# Revit family: Sarlam_Lighting_Bollard_light_Chartres_Infini_T2_Vandal_resistant_Diam_435mm_3000Lm
name_source: partatom
category: Luminaires
units: mm (PartAtom-declared; Revit-internal decimal feet)

## family parameters
Basée sur le plan de construction = Non
Cote de connecteur circulaire = Utiliser le diamètre
Couper avec des vides une fois chargée = Non
Partagée = Non
Point de calcul de pièce = Non
Source d'éclairage = Non
Toujours verticalement = Oui
Type d'élément = Normal

## types (16) — shared parameters
Colour rendering index CRI = 80-89
Colour temperature K MAX = 4000
Colour temperature K MIN = 4000
Effective luminous flux lm = 3000
Fabricant = LEGRAND
General Conditions of Use = https://export.legrand.com
Height/depth = 90 mm  [stored 0.295276 ft]
Lamp holder = None
Lamp power at multiwatt = 21/39W
Lamp type = LED not exchangeable
Length = 435 mm  [stored 1.42717 ft]
Light sharing = Symmetric
Material housing = Plastique
Nominal voltage (Un) V MAX = 253
Nominal voltage (Un) V MIN = 207
Outer diameter = 435 mm  [stored 1.42717 ft]
Protection Class = II
Radiation angle = Open beam
Type of control gear = LED operating device current-controlled
URL = http://www.legrandoc.com
URL Bulkhead = http://www.legrandoc.com
Voltage type = AC
Width = 435 mm  [stored 1.42717 ft]
zero-valued in all types: Elévation par défaut, Nominal current mA MAX, Nominal current mA MIN, System power W

## per-type parameters (varying)
| type | Bollard light Height | Bulkhead | Colour housing | Degree of protection (IP) | Description | Impact strength (IK) | Modèle | Type of dimming | With light sensor | With movement sensor | leg Height |
| Bollard light 600 + ON/OFF WHITE | 600 mm | Legrand-Lighting-Bulkhead-Chartres Infini-T2 Vandal resistant-Diam 435mm-3000Lm : ON/OFF WHITE | LEGRAND - White | IP55 | BOLLARD LIGHT CHARTRES INFINI HEIGHT 600 + CHARTRES INFINI 3000LM 4000K AV ON/OFF WHITE | IK10 | SL-532030 + SL-532015 | Not dimmable | Non | Non | 524 mm |
| Bollard light 1200 + ON/OFF WHITE | 1200 mm | Legrand-Lighting-Bulkhead-Chartres Infini-T2 Vandal resistant-Diam 435mm-3000Lm : ON/OFF WHITE | LEGRAND - White | IP55 | BOLLARD LIGHT CHARTRES INFINI HEIGHT 1200 + CHARTRES INFINI 3000LM 4000K AV ON/OFF WHITE | IK10 | SL-532033 + SL-532015 | Not dimmable | Non | Non | 1124 mm  [stored 3.68766 ft] |
| Bollard light 600 + ON/OFF ANTHRACITE | 600 mm | Legrand-Lighting-Bulkhead-Chartres Infini-T2 Vandal resistant-Diam 435mm-3000Lm : ON/OFF ANTHRACITE | LEGRAND - Anthracite | IP55 | BOLLARD LIGHT CHARTRES INFINI HEIGHT 600 + CHARTRES INFINI 3000LM 4000K AV ON/OFF BLACK | IK10 | SL-532031 + SL-532016 | Not dimmable | Non | Non | 524 mm |
| Bollard light 1200 + ON/OFF ANTHRACITE | 1200 mm | Legrand-Lighting-Bulkhead-Chartres Infini-T2 Vandal resistant-Diam 435mm-3000Lm : ON/OFF ANTHRACITE | LEGRAND - Anthracite | IP55 | BOLLARD LIGHT CHARTRES INFINI HEIGHT 1200 + CHARTRES INFINI 3000LM 4000K AV ON/OFF BLACK | IK10 | SL-532034 + SL-532016 | Not dimmable | Non | Non | 1124 mm  [stored 3.68766 ft] |
| Bollard light 600 + ON/OFF GREY METAL | 600 mm | Legrand-Lighting-Bulkhead-Chartres Infini-T2 Vandal resistant-Diam 435mm-3000Lm : ON/OFF GREY METAL | LEGRAND - Grey | IP55 | BOLLARD LIGHT CHARTRES INFINI HEIGHT 600 + CHARTRES INFINI 3000LM 4000K AV ON/OFF SILVER | IK10 | SL-532032 + SL-532017 | Not dimmable | Non | Non | 524 mm |
| Bollard light 1200 + ON/OFF GREY METAL | 1200 mm | Legrand-Lighting-Bulkhead-Chartres Infini-T2 Vandal resistant-Diam 435mm-3000Lm : ON/OFF GREY METAL | LEGRAND - Grey | IP55 | BOLLARD LIGHT CHARTRES INFINI HEIGHT 1200 + CHARTRES INFINI 3000LM 4000K AV ON/OFF SILVER | IK10 | SL-532035 + SL-532017 | Not dimmable | Non | Non | 1124 mm  [stored 3.68766 ft] |
| Bollard light 600 + With microwave sensor WHITE | 600 mm | Legrand-Lighting-Bulkhead-Chartres Infini-T2 Vandal resistant-Diam 435mm-3000Lm : With microwave sensor WHITE | LEGRAND - White | IP55 | BOLLARD LIGHT CHARTRES INFINI HEIGHT 600 + CHARTRES INFINI 3000LM 4000K AV HF DETECTION WHITE | IK10 | SL-532030 + SL-532055 | Other | Oui | Oui | 524 mm |
| Bollard light 1200 + With microwave sensor WHITE | 1200 mm | Legrand-Lighting-Bulkhead-Chartres Infini-T2 Vandal resistant-Diam 435mm-3000Lm : With microwave sensor WHITE | LEGRAND - White | IP55 | BOLLARD LIGHT CHARTRES INFINI HEIGHT 1200 + CHARTRES INFINI 3000LM 4000K AV HF DETECTION WHITE | IK10 | SL-532033 + SL-532055 | Other | Oui | Oui | 1124 mm  [stored 3.68766 ft] |
| Bollard light 600 + With microwave sensor ANTHRACITE | 600 mm | Legrand-Lighting-Bulkhead-Chartres Infini-T2 Vandal resistant-Diam 435mm-3000Lm : With microwave sensor ANTHRACITE | LEGRAND - Anthracite | IP55 | BOLLARD LIGHT CHARTRES INFINI HEIGHT 600 + CHARTRES INFINI 3000LM 4000K AV HF DETECTION BLACK | IK10 | SL-532031 + SL-532056 | Other | Oui | Oui | 524 mm |
| Bollard light 1200 + With microwave sensor ANTHRACITE | 1200 mm | Legrand-Lighting-Bulkhead-Chartres Infini-T2 Vandal resistant-Diam 435mm-3000Lm : With microwave sensor ANTHRACITE | LEGRAND - Anthracite | IP55 | BOLLARD LIGHT CHARTRES INFINI HEIGHT 1200 + CHARTRES INFINI 3000LM 4000K AV HF DETECTION BLACK | IK10 | SL-532034 + SL-532056 | Other | Oui | Oui | 1124 mm  [stored 3.68766 ft] |
| Bollard light 600 + With microwave sensor GREY METAL | 600 mm | Legrand-Lighting-Bulkhead-Chartres Infini-T2 Vandal resistant-Diam 435mm-3000Lm : With microwave sensor GREY METAL | LEGRAND - Grey | IP55 | BOLLARD LIGHT CHARTRES INFINI HEIGHT 600 + CHARTRES INFINI 3000LM 4000K AV HF DETECTION SILVER | IK10 | SL-532032 + SL-532057 | Other | Oui | Oui | 524 mm |
| Bollard light 1200 + With microwave sensor GREY METAL | 1200 mm | Legrand-Lighting-Bulkhead-Chartres Infini-T2 Vandal resistant-Diam 435mm-3000Lm : With microwave sensor GREY METAL | LEGRAND - Grey | IP55 | BOLLARD LIGHT CHARTRES INFINI HEIGHT 1200 + CHARTRES INFINI 3000LM 4000K AV HF DETECTION SILVER | IK10 | SL-532035 + SL-532057 | Other | Oui | Oui | 1124 mm  [stored 3.68766 ft] |
| Bollard light 1200 + vandal resistant - With microwave sensor | 1200 mm | Legrand-Lighting-Bulkhead-Chartres Infini-T2 Vandal resistant-Diam 435mm-3000Lm : Vandal resistant - With microwave sensor | LEGRAND - White | IP66 | BOLLARD LIGHT CHARTRES INFINI HEIGHT 1200 + CHARTRES INFINI 3000LM 4000K SOLIROC HF DETECTION WHITE | >IK10 | SL-532033 + SL-532099 | Other | Oui | Oui | 1124 mm  [stored 3.68766 ft] |
| Bollard light 600 + vandal resistant - With microwave sensor | 600 mm | Legrand-Lighting-Bulkhead-Chartres Infini-T2 Vandal resistant-Diam 435mm-3000Lm : Vandal resistant - With microwave sensor | LEGRAND - White | IP66 | BOLLARD LIGHT CHARTRES INFINI HEIGHT 600 + CHARTRES INFINI 3000LM 4000K SOLIROC HF DETECTION WHITE | >IK10 | SL-532030 + SL-532099 | Other | Oui | Oui | 524 mm |
| Bollard light 1200 + vandal resistant - ON / OFF | 1200 mm | Legrand-Lighting-Bulkhead-Chartres Infini-T2 Vandal resistant-Diam 435mm-3000Lm : Vandal resistant-ON/OFF | LEGRAND - White | IP66 | BOLLARD LIGHT CHARTRES INFINI HEIGHT 1200 + BLACK CHARTRES INFINI 3000LM 4000K SOLIROC ON/OFF WHITE | >IK10 | SL-532033 + SL-532098 | Not dimmable | Non | Non | 1124 mm  [stored 3.68766 ft] |
| Bollard light 600 + vandal resistant - ON / OFF | 600 mm | Legrand-Lighting-Bulkhead-Chartres Infini-T2 Vandal resistant-Diam 435mm-3000Lm : Vandal resistant-ON/OFF | LEGRAND - White | IP66 | BOLLARD LIGHT CHARTRES INFINI HEIGHT 600 + BLACK CHARTRES INFINI 3000LM 4000K SOLIROC ON/OFF WHITE | >IK10 | SL-532030 + SL-532098 | Not dimmable | Non | Non | 524 mm |

note: [stored X ft] marks values corroborated as IEEE doubles in the binary element streams (Revit-internal decimal feet)

## geometry (parser evidence)
native form markers: Blend x14
no freeform markers — native parametric forms only
